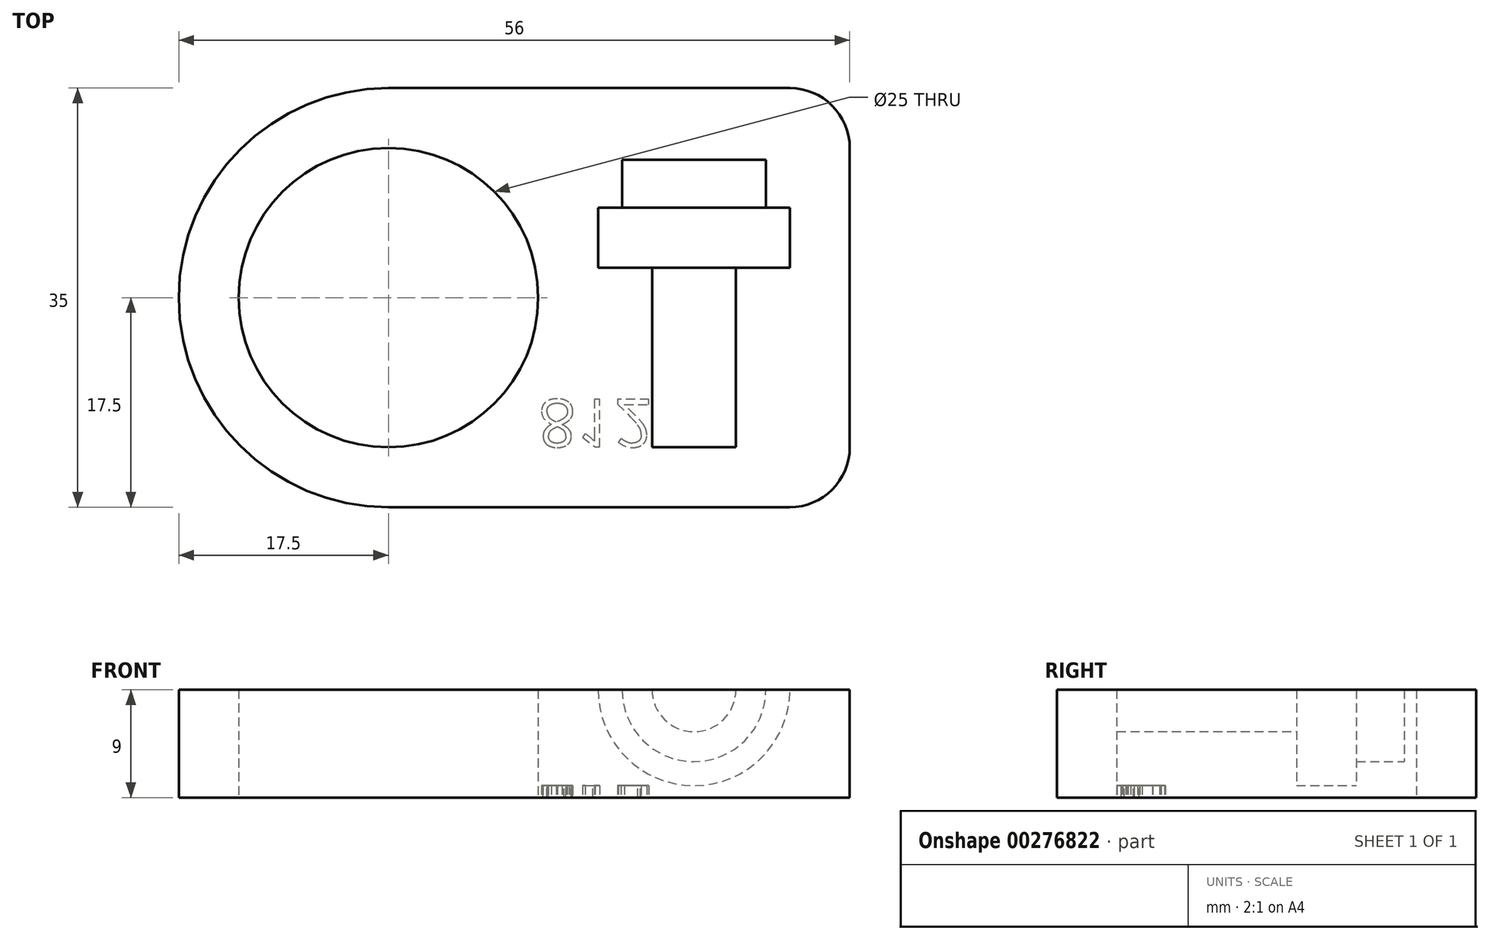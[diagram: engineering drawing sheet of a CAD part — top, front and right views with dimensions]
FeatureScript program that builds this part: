
annotation { "Feature Type Name" : "Feature", "Feature Type Description" : "" }
export const myFeature = defineFeature(function(context is Context, id is Id, definition is map)
    precondition{}
    {
        {
            var Q0;
            Q0=qCreatedBy(makeId("Top.planeOp"),FACE);
            var sketch = newSketch(context, id + "F0", { "sketchPlane" : qUnion([Q0])});
            skLineSegment(sketch, "E0.bottom", {"start": v(17.5, 0) * mm, "end": v(51, 0) * mm});
            skLineSegment(sketch, "E0.top", {"start": v(17.5, 35) * mm, "end": v(51, 35) * mm});
            skLineSegment(sketch, "E0.left", {"start": v(0, 17.5) * mm, "end": v(0, 17.5) * mm});
            skLineSegment(sketch, "E0.right", {"start": v(56, 5) * mm, "end": v(56, 30) * mm});
            skLineSegment(sketch, "E1.bottom", {"start": v(0, 0) * mm, "end": v(17.5, 0) * mm, "construction": true});
            skLineSegment(sketch, "E1.top", {"start": v(0, 17.5) * mm, "end": v(17.5, 17.5) * mm, "construction": true});
            skLineSegment(sketch, "E1.left", {"start": v(0, 0) * mm, "end": v(0, 17.5) * mm, "construction": true});
            skLineSegment(sketch, "E1.right", {"start": v(17.5, 0) * mm, "end": v(17.5, 17.5) * mm, "construction": true});
            skCircle(sketch, "E2", {"center": v(17.5, 17.5) * mm, "radius": 12.5 * mm});
            skPoint(sketch, "E3.visualSharp", {"position": v(0, 0) * mm});
            skArc(sketch, "E3.filletArc", {"start": v(0, 17.5) * mm, "mid": v(5.13, 5.13) * mm, "end": v(17.5, 0) * mm});
            skPoint(sketch, "E4.visualSharp", {"position": v(0, 35) * mm});
            skArc(sketch, "E4.filletArc", {"start": v(17.5, 35) * mm, "mid": v(5.13, 29.87) * mm, "end": v(0, 17.5) * mm});
            skPoint(sketch, "E5.visualSharp", {"position": v(56, 35) * mm});
            skArc(sketch, "E5.filletArc", {"start": v(56, 30) * mm, "mid": v(54.54, 33.54) * mm, "end": v(51, 35) * mm});
            skPoint(sketch, "E6.visualSharp", {"position": v(56, 0) * mm});
            skArc(sketch, "E6.filletArc", {"start": v(51, 0) * mm, "mid": v(54.54, 1.46) * mm, "end": v(56, 5) * mm});
            skSolve(sketch);
        }
        {
            var Q0;
            Q0=makeQuery(id+"F0.imprint","IMPRINT",FACE,{"disambiguationData":[TD([[makeQuery(id+"F0.imprint","IMPRINT",EDGE,{"derivedFrom":sQuery(id+"F0.wireOp",EDGE,"E0.bottom")}),1.0]])]});
            extrude(context, id + "F1", {"entities" : qUnion([Q0]), "depth" : 9 * mm});
        }
        {
            var Q0;
            Q0=makeQuery(id+"F1.opExtrude","CAP_FACE",FACE,{"disambiguationData":[OSD([sQuery(id+"F0.wireOp",EDGE,"E0.bottom"),sQuery(id+"F0.wireOp",EDGE,"E0.top"),sQuery(id+"F0.wireOp",EDGE,"E0.right"),sQuery(id+"F0.wireOp",EDGE,"E2"),sQuery(id+"F0.wireOp",EDGE,"E3.filletArc"),sQuery(id+"F0.wireOp",EDGE,"E4.filletArc"),sQuery(id+"F0.wireOp",EDGE,"E5.filletArc"),sQuery(id+"F0.wireOp",EDGE,"E6.filletArc")])],"isStart":false});
            var sketch = newSketch(context, id + "F2", { "sketchPlane" : qUnion([Q0])});
            skLineSegment(sketch, "E7.bottom", {"start": v(0, 0) * mm, "end": v(43, 0) * mm, "construction": true});
            skLineSegment(sketch, "E7.top", {"start": v(0, 5) * mm, "end": v(43, 5) * mm, "construction": true});
            skLineSegment(sketch, "E7.left", {"start": v(0, 0) * mm, "end": v(0, 5) * mm, "construction": true});
            skLineSegment(sketch, "E7.right", {"start": v(43, 0) * mm, "end": v(43, 5) * mm, "construction": true});
            skLineSegment(sketch, "E8.bottom", {"start": v(43, 5) * mm, "end": v(46.5, 5) * mm});
            skLineSegment(sketch, "E8.left", {"start": v(43, 5) * mm, "end": v(43, 20) * mm});
            skLineSegment(sketch, "E8.right", {"start": v(46.5, 5) * mm, "end": v(46.5, 20) * mm});
            skLineSegment(sketch, "E9.bottom", {"start": v(46.5, 20) * mm, "end": v(51, 20) * mm});
            skLineSegment(sketch, "E9.top", {"start": v(49, 25) * mm, "end": v(51, 25) * mm});
            skLineSegment(sketch, "E9.left", {"start": v(43, 20) * mm, "end": v(43, 25) * mm});
            skLineSegment(sketch, "E9.right", {"start": v(51, 20) * mm, "end": v(51, 25) * mm});
            skLineSegment(sketch, "E10.top", {"start": v(43, 29) * mm, "end": v(49, 29) * mm});
            skLineSegment(sketch, "E10.left", {"start": v(43, 25) * mm, "end": v(43, 29) * mm});
            skLineSegment(sketch, "E10.right", {"start": v(49, 25) * mm, "end": v(49, 29) * mm});
            skSolve(sketch);
        }
        {
            var Q0;
            Q0=makeQuery(id+"F2.imprint","IMPRINT",FACE,{"disambiguationData":[TD([[makeQuery(id+"F2.imprint","IMPRINT",EDGE,{"derivedFrom":sQuery(id+"F2.wireOp",EDGE,"E8.bottom")}),1.0]])]});
            var Q1;
            Q1=sQuery(id+"F2.wireOp",EDGE,"E8.left");
            revolve(context, id + "F3", {"operationType" : NewBodyOperationType.REMOVE, "entities" : qUnion([Q0]), "axis" : qUnion([Q1]), "revolveType" : RevolveType.FULL, "oppositeDirection" : true});
        }
        {
            var Q0;
            Q0=makeQuery(id+"F1.opExtrude","CAP_FACE",FACE,{"disambiguationData":[OSD([sQuery(id+"F0.wireOp",EDGE,"E0.bottom"),sQuery(id+"F0.wireOp",EDGE,"E0.top"),sQuery(id+"F0.wireOp",EDGE,"E0.right"),sQuery(id+"F0.wireOp",EDGE,"E2"),sQuery(id+"F0.wireOp",EDGE,"E3.filletArc"),sQuery(id+"F0.wireOp",EDGE,"E4.filletArc"),sQuery(id+"F0.wireOp",EDGE,"E5.filletArc"),sQuery(id+"F0.wireOp",EDGE,"E6.filletArc")])],"isStart":true});
            var sketch = newSketch(context, id + "F4", { "sketchPlane" : qUnion([Q0])});
            skLineSegment(sketch, "E11.bottom", {"start": v(0, 0) * mm, "end": v(30, 0) * mm, "construction": true});
            skLineSegment(sketch, "E11.top", {"start": v(0, -5) * mm, "end": v(30, -5) * mm, "construction": true});
            skLineSegment(sketch, "E11.left", {"start": v(0, 0) * mm, "end": v(0, -5) * mm, "construction": true});
            skLineSegment(sketch, "E11.right", {"start": v(30, 0) * mm, "end": v(30, -5) * mm, "construction": true});
            skText(sketch, "E12", { "text": "812", "fontName": "OpenSans-Regular.ttf"});
            const initialGuessF4  = {"E12": [0.03, -0.009, 1, 0, 0.004]};
            skSetInitialGuess(sketch, initialGuessF4);
            skSolve(sketch);
        }
        {
            var Q0;
            Q0 = qSketchRegion(id + "F4", true);
            extrude(context, id + "F5", {"entities" : qUnion([Q0]), "operationType" : NewBodyOperationType.REMOVE, "oppositeDirection" : true, "depth" : 1 * mm});
        }
    });
